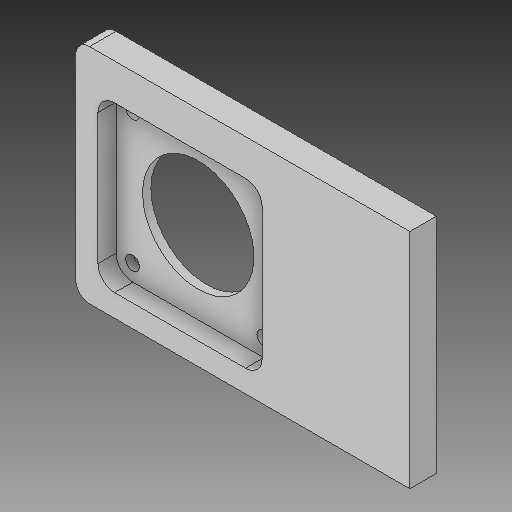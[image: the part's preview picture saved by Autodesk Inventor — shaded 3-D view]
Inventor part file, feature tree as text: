
AUTODESK INVENTOR PART (.ipt)
format: ipt  version: 2018 (Build 220112000, 112)  size: 135,680 bytes
history: native  units: mm
features: other x4, sketch x3
ambient origin geometry x8: Origin, YZ Plane, XZ Plane, XY Plane, X Axis, Y Axis, Z Axis, Center Point
bodies: Body1 (feature_tree)
feature tree (7):
  other  "SUPORTE_MOTOR_EIXO_Y_1.ipt"
  other  "Sólido1::SUPORTE_MOTOR_EIXO_Y_1.ipt"
  other  "OperaçãoIdentificador1"
  sketch  "Esboço1"  dims[d0=10.0mm]
  sketch  "Esboço9"
  sketch  "Esboço10"
  other  "Sólido1"
